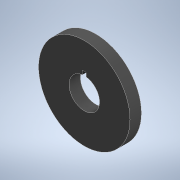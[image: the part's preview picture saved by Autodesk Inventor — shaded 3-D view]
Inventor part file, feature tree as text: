
AUTODESK INVENTOR PART (.ipt)
format: ipt  version: 2021 (Build 250183000, 183)  size: 108,032 bytes
history: native  units: in
note: dims shown in document units (in); Inventor stores cm internally (conversion verified against a paired STEP export)
features: extrude x1, sketch x1
ambient origin geometry x8: Origin, YZ Plane, XZ Plane, XY Plane, X Axis, Y Axis, Z Axis, Center Point
bodies: Body1 (feature_tree)
feature tree (2):
  extrude  "Extrusion4"  Depth=0.375in
  sketch  "Sketch5"  dims[d11=3.0in d12=1.0in d13=1.25in d14=0.0625in d15=0.0625in d16=0.375in d17=0.0in]
